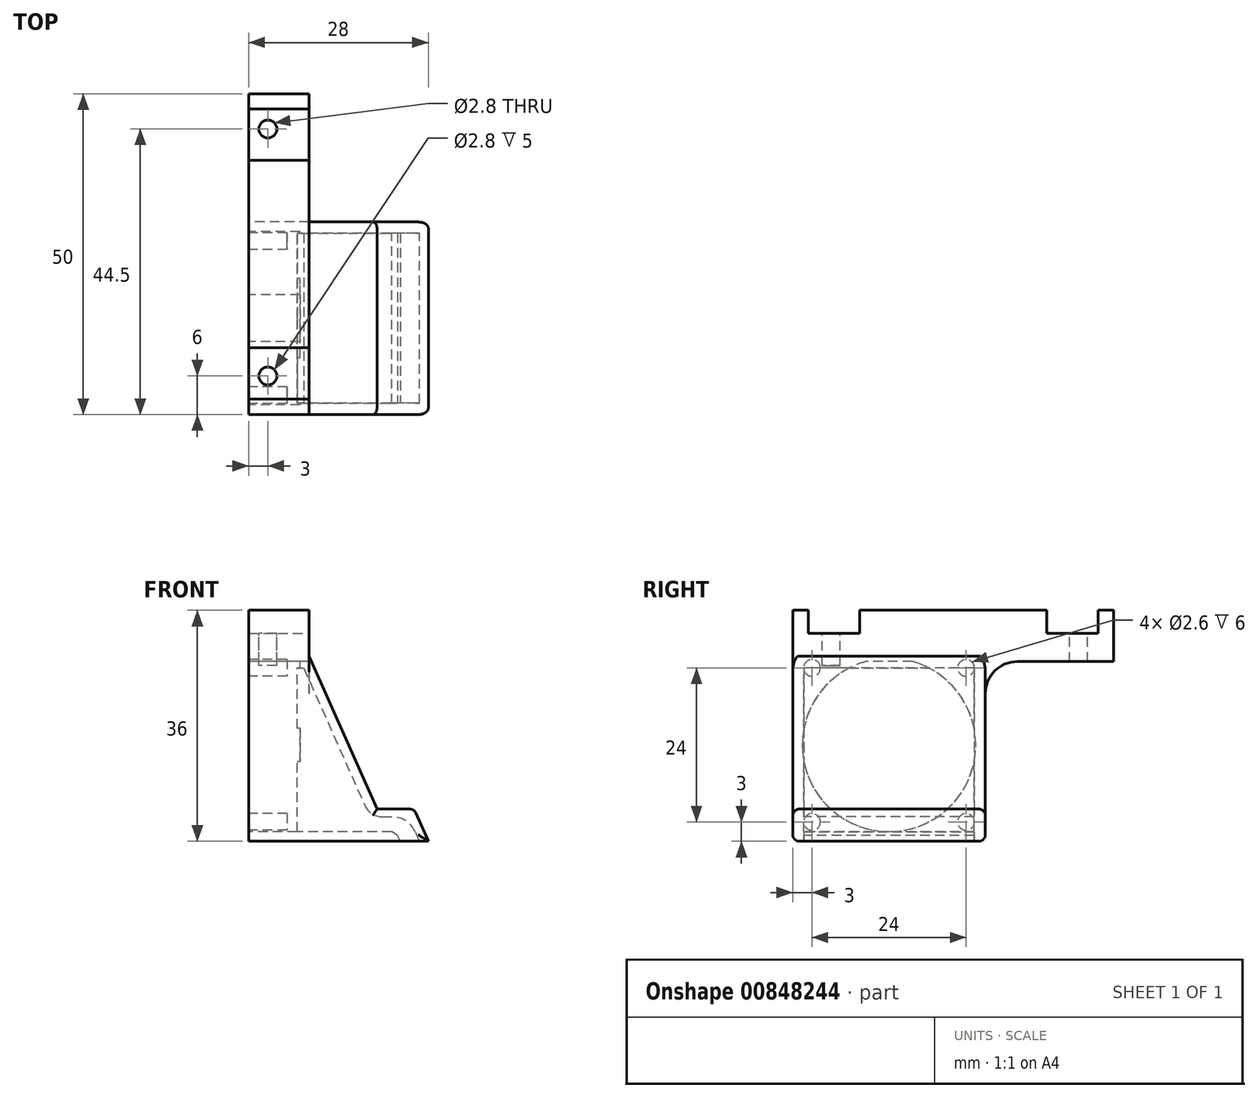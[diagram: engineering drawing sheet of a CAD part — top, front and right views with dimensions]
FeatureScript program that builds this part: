
annotation { "Feature Type Name" : "Feature", "Feature Type Description" : "" }
export const myFeature = defineFeature(function(context is Context, id is Id, definition is map)
    precondition{}
    {
        {
            var Q0;
            Q0=qCreatedBy(makeId("Front.planeOp"),FACE);
            var sketch = newSketch(context, id + "F0", { "sketchPlane" : qUnion([Q0])});
            skLineSegment(sketch, "E0", {"start": v(0, 0) * mm, "end": v(0, 32) * mm});
            skLineSegment(sketch, "E1", {"start": v(0, 32) * mm, "end": v(8, 32) * mm});
            skLineSegment(sketch, "E2", {"start": v(8, 32) * mm, "end": v(20, 5) * mm});
            skLineSegment(sketch, "E3", {"start": v(28, 0) * mm, "end": v(0, 0) * mm});
            skLineSegment(sketch, "E4", {"start": v(20, 5) * mm, "end": v(25.78, 5) * mm});
            skLineSegment(sketch, "E5", {"start": v(25.78, 5) * mm, "end": v(28, 0) * mm});
            skSolve(sketch);
        }
        {
            var Q0;
            Q0=makeQuery(id+"F0.imprint","IMPRINT",FACE,{"disambiguationData":[TD([[makeQuery(id+"F0.imprint","IMPRINT",EDGE,{"derivedFrom":sQuery(id+"F0.wireOp",EDGE,"E0")}),-1.0]])]});
            extrude(context, id + "F1", {"entities" : qUnion([Q0]), "depth" : 30 * mm, "offsetDistance" : 25 * mm});
        }
        {
            var Q0;
            Q0=makeQuery(id+"F1.opExtrude","SWEPT_FACE",FACE,{"disambiguationData":[OSD([sQuery(id+"F0.wireOp",EDGE,"E1")])]});
            var sketch = newSketch(context, id + "F2", { "sketchPlane" : qUnion([Q0])});
            skLineSegment(sketch, "E6.bottom", {"start": v(0, -30) * mm, "end": v(9.4, -30) * mm});
            skLineSegment(sketch, "E6.top", {"start": v(0, 20) * mm, "end": v(9.4, 20) * mm});
            skLineSegment(sketch, "E6.left", {"start": v(0, -30) * mm, "end": v(0, 20) * mm});
            skLineSegment(sketch, "E6.right", {"start": v(9.4, -30) * mm, "end": v(9.4, 20) * mm});
            skSolve(sketch);
        }
        {
            var Q0;
            Q0 = qSketchRegion(id + "F2", true);
            extrude(context, id + "F3", {"entities" : qUnion([Q0]), "operationType" : NewBodyOperationType.ADD, "endBound" : BoundingType.SYMMETRIC, "oppositeDirection" : true, "depth" : 8 * mm, "offsetDistance" : 25 * mm});
        }
        {
            var Q0;
            Q0=qCreatedBy(makeId("Top.planeOp"),FACE);
            cPlane(context, id + "F4", {"entities" : qUnion([Q0]), "cplaneType" : CPlaneType.OFFSET, "offset" : 36 * mm, "width" : 150 * mm, "height" : 150 * mm});
        }
        {
            var Q0;
            Q0=qCreatedBy(id+"F4.planeOp",FACE);
            var sketch = newSketch(context, id + "F5", { "sketchPlane" : qUnion([Q0])});
            skLineSegment(sketch, "E7.bottom", {"start": v(0, 17.6) * mm, "end": v(10, 17.6) * mm});
            skLineSegment(sketch, "E7.top", {"start": v(0, 9.6) * mm, "end": v(10, 9.6) * mm});
            skLineSegment(sketch, "E7.left", {"start": v(0, 17.6) * mm, "end": v(0, 9.6) * mm});
            skLineSegment(sketch, "E7.right", {"start": v(10, 17.6) * mm, "end": v(10, 9.6) * mm});
            skLineSegment(sketch, "E8.bottom", {"start": v(0, -19.6) * mm, "end": v(12, -19.6) * mm});
            skLineSegment(sketch, "E8.top", {"start": v(0, -27.6) * mm, "end": v(12, -27.6) * mm});
            skLineSegment(sketch, "E8.left", {"start": v(0, -19.6) * mm, "end": v(0, -27.6) * mm});
            skLineSegment(sketch, "E8.right", {"start": v(12, -19.6) * mm, "end": v(12, -27.6) * mm});
            skSolve(sketch);
        }
        {
            var Q0;
            Q0=makeQuery(id+"F5.imprint","IMPRINT",FACE,{"disambiguationData":[TD([[makeQuery(id+"F5.imprint","IMPRINT",EDGE,{"derivedFrom":sQuery(id+"F5.wireOp",EDGE,"E7.bottom")}),-1.0]])]});
            var Q1;
            Q1=makeQuery(id+"F5.imprint","IMPRINT",FACE,{"disambiguationData":[TD([[makeQuery(id+"F5.imprint","IMPRINT",EDGE,{"derivedFrom":sQuery(id+"F5.wireOp",EDGE,"E8.bottom")}),-1.0]])]});
            extrude(context, id + "F6", {"entities" : qUnion([Q0, Q1]), "operationType" : NewBodyOperationType.REMOVE, "oppositeDirection" : true, "depth" : 3.6 * mm, "offsetDistance" : 25 * mm});
        }
        {
            var Q0;
            Q0=qCreatedBy(makeId("Front.planeOp"),FACE);
            cPlane(context, id + "F7", {"entities" : qUnion([Q0]), "cplaneType" : CPlaneType.OFFSET, "offset" : 28.25 * mm, "width" : 150 * mm, "height" : 150 * mm});
        }
        {
            var Q0;
            Q0=qCreatedBy(id+"F7.planeOp",FACE);
            var sketch = newSketch(context, id + "F8", { "sketchPlane" : qUnion([Q0])});
            skLineSegment(sketch, "E9", {"start": v(8.58, 27) * mm, "end": v(18.9, 3.8) * mm});
            skLineSegment(sketch, "E10", {"start": v(27.5, -2) * mm, "end": v(24.5, -2) * mm});
            skLineSegment(sketch, "E11", {"start": v(24.5, -2) * mm, "end": v(22.94, 1.5) * mm});
            skLineSegment(sketch, "E12", {"start": v(22.94, 1.5) * mm, "end": v(7.58, 1.5) * mm});
            skLineSegment(sketch, "E13", {"start": v(7.58, 1.5) * mm, "end": v(7.58, 27) * mm});
            skLineSegment(sketch, "E14", {"start": v(7.58, 27) * mm, "end": v(8.58, 27) * mm});
            skLineSegment(sketch, "E15", {"start": v(18.9, 3.8) * mm, "end": v(24.92, 3.8) * mm});
            skLineSegment(sketch, "E16", {"start": v(24.92, 3.8) * mm, "end": v(27.5, -2) * mm});
            skSolve(sketch);
        }
        {
            var Q0;
            Q0 = qSketchRegion(id + "F8", true);
            extrude(context, id + "F9", {"entities" : qUnion([Q0]), "operationType" : NewBodyOperationType.REMOVE, "oppositeDirection" : true, "depth" : 26.5 * mm, "offsetDistance" : 25 * mm});
        }
        {
            var Q0;
            Q0=makeQuery(id+"F3.boolean.opBoolean","MERGE",FACE,{"derivedFrom":[makeQuery(id+"F1.opExtrude","SWEPT_FACE",FACE,{"disambiguationData":[OSD([sQuery(id+"F0.wireOp",EDGE,"E0")])]}),makeQuery(id+"F3.opExtrude","SWEPT_FACE",FACE,{"disambiguationData":[OSD([sQuery(id+"F2.wireOp",EDGE,"E6.left")])]})]});
            var sketch = newSketch(context, id + "F10", { "sketchPlane" : qUnion([Q0])});
            skArc(sketch, "E17", {"start": v(11.36, 28) * mm, "mid": v(15, 1.5) * mm, "end": v(18.64, 28) * mm});
            skLineSegment(sketch, "E18", {"start": v(11.36, 28) * mm, "end": v(18.64, 28) * mm});
            skSolve(sketch);
        }
        {
            var Q0;
            Q0=makeQuery(id+"F10.imprint","IMPRINT",FACE,{"disambiguationData":[TD([[makeQuery(id+"F10.imprint","IMPRINT",EDGE,{"derivedFrom":sQuery(id+"F10.wireOp",EDGE,"E17")}),1.0]])]});
            extrude(context, id + "F11", {"entities" : qUnion([Q0]), "operationType" : NewBodyOperationType.REMOVE, "oppositeDirection" : true, "depth" : 8 * mm, "offsetDistance" : 25 * mm});
        }
        {
            var Q0;
            Q0=makeQuery(id+"F3.boolean.opBoolean","MERGE",FACE,{"derivedFrom":[makeQuery(id+"F1.opExtrude","SWEPT_FACE",FACE,{"disambiguationData":[OSD([sQuery(id+"F0.wireOp",EDGE,"E0")])]}),makeQuery(id+"F3.opExtrude","SWEPT_FACE",FACE,{"disambiguationData":[OSD([sQuery(id+"F2.wireOp",EDGE,"E6.left")])]})]});
            var sketch = newSketch(context, id + "F12", { "sketchPlane" : qUnion([Q0])});
            skCircle(sketch, "E19", {"center": v(3, 27) * mm, "radius": 1.3 * mm});
            skCircle(sketch, "E20", {"center": v(3, 3) * mm, "radius": 1.3 * mm});
            skCircle(sketch, "E21", {"center": v(27, 3) * mm, "radius": 1.3 * mm});
            skCircle(sketch, "E22", {"center": v(27, 27) * mm, "radius": 1.3 * mm});
            skSolve(sketch);
        }
        {
            var Q0;
            Q0 = qSketchRegion(id + "F12", true);
            extrude(context, id + "F13", {"entities" : qUnion([Q0]), "operationType" : NewBodyOperationType.REMOVE, "oppositeDirection" : true, "depth" : 6 * mm, "offsetDistance" : 25 * mm});
        }
        {
            var Q0;
            Q0=makeQuery(id+"F6.boolean.opBoolean","COPY",FACE,{"derivedFrom":makeQuery(id+"F6.opExtrude","CAP_FACE",FACE,{"disambiguationData":[OSD([sQuery(id+"F5.wireOp",EDGE,"E7.bottom"),sQuery(id+"F5.wireOp",EDGE,"E7.top"),sQuery(id+"F5.wireOp",EDGE,"E7.left"),sQuery(id+"F5.wireOp",EDGE,"E7.right")])],"isStart":false})});
            var sketch = newSketch(context, id + "F14", { "sketchPlane" : qUnion([Q0])});
            skCircle(sketch, "E23", {"center": v(3, 14.5) * mm, "radius": 1.4 * mm});
            skSolve(sketch);
        }
        {
            var Q0;
            Q0=makeQuery(id+"F6.boolean.opBoolean","COPY",FACE,{"derivedFrom":makeQuery(id+"F6.opExtrude","CAP_FACE",FACE,{"disambiguationData":[OSD([sQuery(id+"F5.wireOp",EDGE,"E8.bottom"),sQuery(id+"F5.wireOp",EDGE,"E8.top"),sQuery(id+"F5.wireOp",EDGE,"E8.left"),sQuery(id+"F5.wireOp",EDGE,"E8.right")])],"isStart":false})});
            var sketch = newSketch(context, id + "F15", { "sketchPlane" : qUnion([Q0])});
            skCircle(sketch, "E24", {"center": v(3, -24) * mm, "radius": 1.4 * mm});
            skSolve(sketch);
        }
        {
            var Q0;
            Q0 = qSketchRegion(id + "F14", true);
            extrude(context, id + "F16", {"entities" : qUnion([Q0]), "operationType" : NewBodyOperationType.REMOVE, "oppositeDirection" : true, "depth" : 5 * mm, "offsetDistance" : 25 * mm});
        }
        {
            var Q0;
            Q0 = qSketchRegion(id + "F15", true);
            extrude(context, id + "F17", {"entities" : qUnion([Q0]), "operationType" : NewBodyOperationType.REMOVE, "oppositeDirection" : true, "depth" : 5 * mm, "offsetDistance" : 25 * mm});
        }
        {
            var Q0;
            Q0=makeQuery(id+"F9.boolean.opBoolean","COPY",EDGE,{"derivedFrom":makeQuery(id+"F9.opExtrude","SWEPT_EDGE",EDGE,{"disambiguationData":[OSD([sQuery(id+"F8.wireOp",EDGE,"E9"),sQuery(id+"F8.wireOp",EDGE,"E15")])]})});
            fillet(context, id + "F18", {"entities" : qUnion([Q0]), "radius" : 3 * mm, "tangentPropagation" : true, "allowEdgeOverflow" : false});
        }
        {
            var Q0;
            Q0=makeQuery(id+"F9.boolean.opBoolean","COPY",EDGE,{"derivedFrom":makeQuery(id+"F9.opExtrude","SWEPT_EDGE",EDGE,{"disambiguationData":[OSD([sQuery(id+"F8.wireOp",EDGE,"E15"),sQuery(id+"F8.wireOp",EDGE,"E16")])]})});
            fillet(context, id + "F19", {"entities" : qUnion([Q0]), "radius" : 4 * mm, "tangentPropagation" : true, "allowEdgeOverflow" : false});
        }
        {
            var Q0;
            Q0=makeQuery(id+"F9.boolean.opBoolean","COPY",EDGE,{"derivedFrom":makeQuery(id+"F9.opExtrude","SWEPT_EDGE",EDGE,{"disambiguationData":[OSD([sQuery(id+"F8.wireOp",EDGE,"E11"),sQuery(id+"F8.wireOp",EDGE,"E12")])]})});
            chamfer(context, id + "F20", {"entities" : qUnion([Q0]), "width" : 1 * mm, "tangentPropagation" : true});
        }
        {
            var Q0;
            Q0=makeQuery(id+"F1.opExtrude","CAP_EDGE",EDGE,{"disambiguationData":[OSD([sQuery(id+"F0.wireOp",EDGE,"E3")])],"isStart":false});
            var Q1;
            Q1=makeQuery(id+"F1.opExtrude","CAP_EDGE",EDGE,{"disambiguationData":[OSD([sQuery(id+"F0.wireOp",EDGE,"E2")])],"isStart":false});
            var Q2;
            Q2=makeQuery(id+"F1.opExtrude","CAP_EDGE",EDGE,{"disambiguationData":[OSD([sQuery(id+"F0.wireOp",EDGE,"E4")])],"isStart":false});
            var Q3;
            Q3=makeQuery(id+"F1.opExtrude","CAP_EDGE",EDGE,{"disambiguationData":[OSD([sQuery(id+"F0.wireOp",EDGE,"E5")])],"isStart":false});
            var Q4;
            Q4=makeQuery(id+"F1.opExtrude","CAP_EDGE",EDGE,{"disambiguationData":[OSD([sQuery(id+"F0.wireOp",EDGE,"E2")])],"isStart":true});
            var Q5;
            Q5=makeQuery(id+"F1.opExtrude","CAP_EDGE",EDGE,{"disambiguationData":[OSD([sQuery(id+"F0.wireOp",EDGE,"E4")])],"isStart":true});
            var Q6;
            Q6=makeQuery(id+"F1.opExtrude","CAP_EDGE",EDGE,{"disambiguationData":[OSD([sQuery(id+"F0.wireOp",EDGE,"E5")])],"isStart":true});
            var Q7;
            Q7=makeQuery(id+"F1.opExtrude","CAP_EDGE",EDGE,{"disambiguationData":[OSD([sQuery(id+"F0.wireOp",EDGE,"E3")])],"isStart":true});
            var Q8;
            Q8=makeQuery(id+"F1.opExtrude","SWEPT_EDGE",EDGE,{"disambiguationData":[OSD([sQuery(id+"F0.wireOp",EDGE,"E4"),sQuery(id+"F0.wireOp",EDGE,"E5")])]});
            fillet(context, id + "F21", {"entities" : qUnion([Q0, Q1, Q2, Q3, Q4, Q5, Q6, Q7, Q8]), "radius" : 1 * mm, "tangentPropagation" : true, "allowEdgeOverflow" : false});
        }
        {
            var Q0;
            Q0=makeQuery(id+"F3.boolean.opBoolean","INTERSECT",EDGE,{"derivedFrom":[makeQuery(id+"F1.opExtrude","CAP_FACE",FACE,{"disambiguationData":[OSD([sQuery(id+"F0.wireOp",EDGE,"E0"),sQuery(id+"F0.wireOp",EDGE,"E1"),sQuery(id+"F0.wireOp",EDGE,"E2"),sQuery(id+"F0.wireOp",EDGE,"E3"),sQuery(id+"F0.wireOp",EDGE,"E4"),sQuery(id+"F0.wireOp",EDGE,"E5")])],"isStart":true}),makeQuery(id+"F3.opExtrude","CAP_FACE",FACE,{"disambiguationData":[OSD([sQuery(id+"F2.wireOp",EDGE,"E6.bottom"),sQuery(id+"F2.wireOp",EDGE,"E6.top"),sQuery(id+"F2.wireOp",EDGE,"E6.left"),sQuery(id+"F2.wireOp",EDGE,"E6.right")])],"isStart":false})]});
            fillet(context, id + "F22", {"entities" : qUnion([Q0]), "radius" : 5 * mm, "tangentPropagation" : true, "allowEdgeOverflow" : false});
        }
    });
